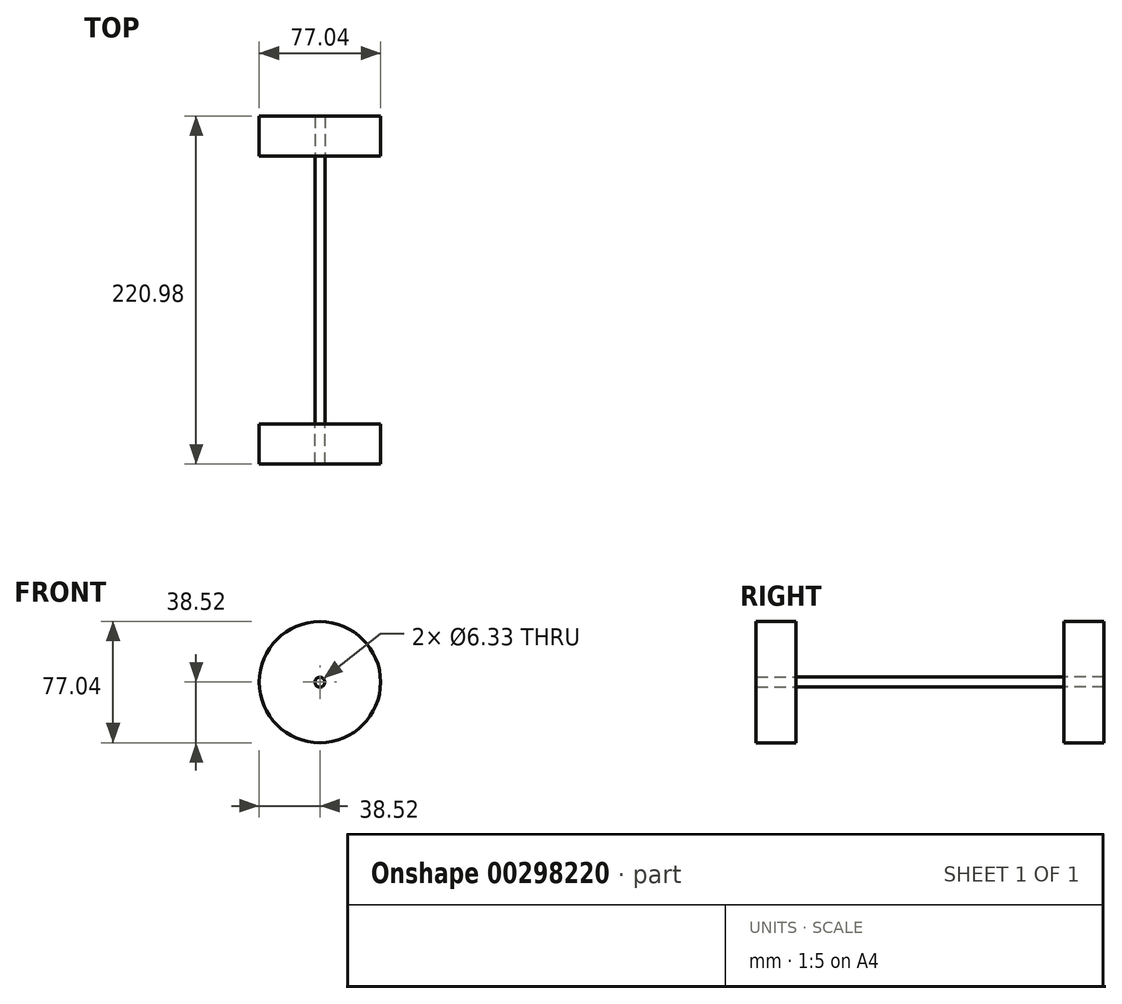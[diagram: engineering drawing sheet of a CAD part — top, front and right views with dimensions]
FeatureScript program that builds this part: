
annotation { "Feature Type Name" : "Feature", "Feature Type Description" : "" }
export const myFeature = defineFeature(function(context is Context, id is Id, definition is map)
    precondition{}
    {
        {
            var Q0;
            Q0=qCreatedBy(makeId("Front.planeOp"),FACE);
            var sketch = newSketch(context, id + "F0", { "sketchPlane" : qUnion([Q0])});
            skCircle(sketch, "E0", {"center": v(0, 0) * mm, "radius": 3.16 * mm});
            skSolve(sketch);
        }
        {
            var Q0;
            Q0=makeQuery(id+"F0.imprint","IMPRINT",FACE,{"disambiguationData":[TD([[makeQuery(id+"F0.imprint","IMPRINT",EDGE,{"derivedFrom":sQuery(id+"F0.wireOp",EDGE,"E0")}),1.0]])]});
            extrude(context, id + "F1", {"entities" : qUnion([Q0]), "depth" : 170.18 * mm});
        }
        {
            var Q0;
            Q0=makeQuery(id+"F1.opExtrude","CAP_FACE",FACE,{"disambiguationData":[OSD([sQuery(id+"F0.wireOp",EDGE,"E0")])],"isStart":false});
            var sketch = newSketch(context, id + "F2", { "sketchPlane" : qUnion([Q0])});
            skCircle(sketch, "E1", {"center": v(0, 0) * mm, "radius": 38.52 * mm});
            skSolve(sketch);
        }
        {
            var Q0;
            Q0=makeQuery(id+"F1.opExtrude","CAP_FACE",FACE,{"disambiguationData":[OSD([sQuery(id+"F0.wireOp",EDGE,"E0")])],"isStart":true});
            var sketch = newSketch(context, id + "F3", { "sketchPlane" : qUnion([Q0])});
            skCircle(sketch, "E2", {"center": v(0, 0) * mm, "radius": 38.52 * mm});
            skSolve(sketch);
        }
        {
            var Q0;
            Q0=makeQuery(id+"F3.imprint","IMPRINT",FACE,{"disambiguationData":[TD([[makeQuery(id+"F3.imprint","IMPRINT",EDGE,{"derivedFrom":sQuery(id+"F3.wireOp",EDGE,"E2")}),1.0]])]});
            extrude(context, id + "F4", {"entities" : qUnion([Q0]), "depth" : 25.4 * mm});
        }
        {
            var Q0;
            Q0=makeQuery(id+"F2.imprint","IMPRINT",FACE,{"disambiguationData":[TD([[makeQuery(id+"F2.imprint","IMPRINT",EDGE,{"derivedFrom":sQuery(id+"F2.wireOp",EDGE,"E1")}),1.0]])]});
            extrude(context, id + "F5", {"entities" : qUnion([Q0]), "depth" : 25.4 * mm});
        }
    });
